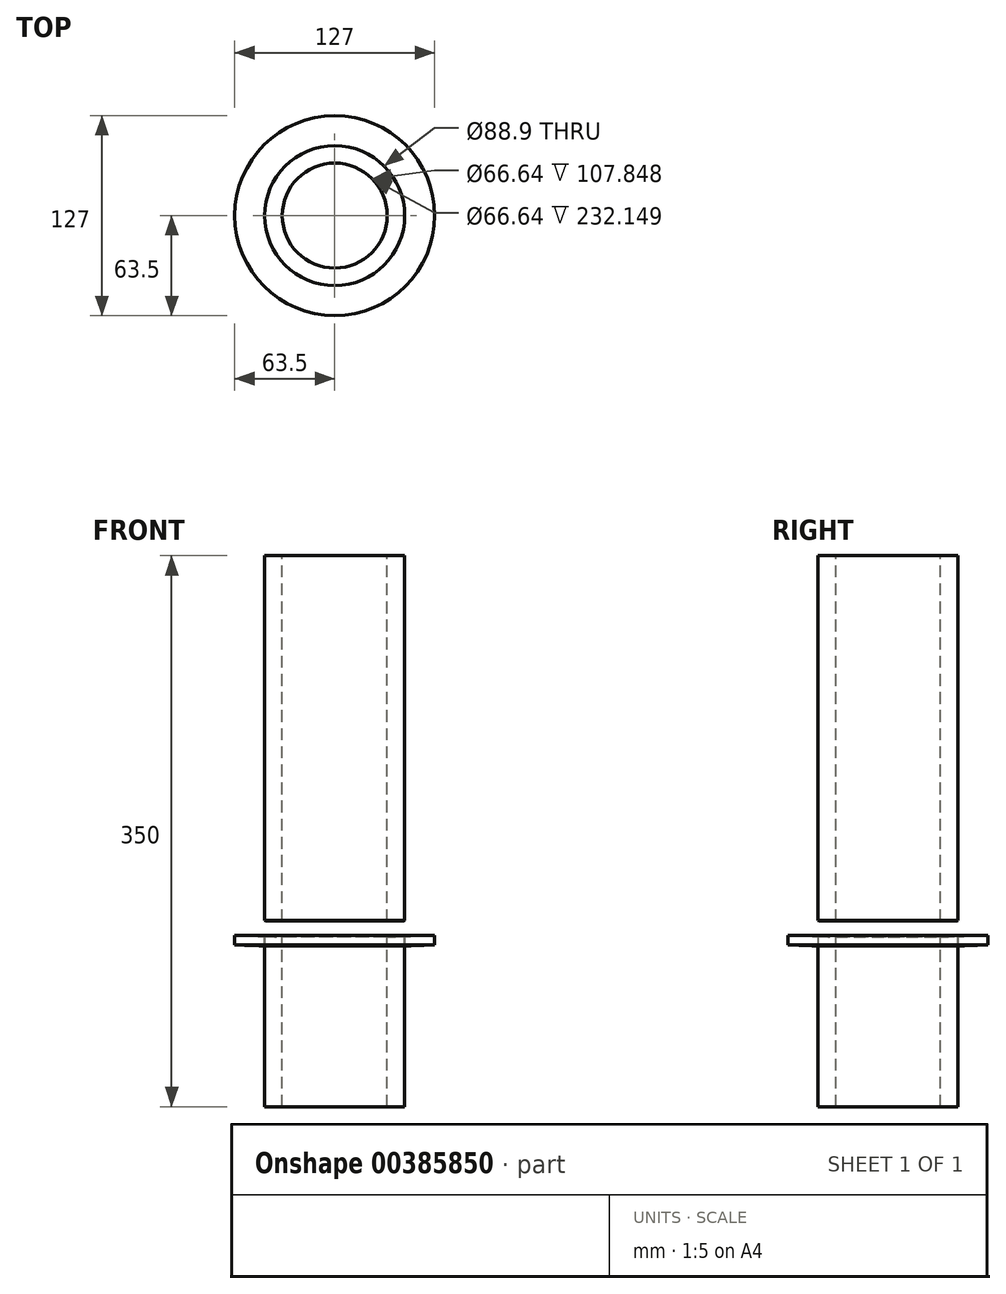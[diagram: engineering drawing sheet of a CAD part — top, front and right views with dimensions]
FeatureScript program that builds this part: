
annotation { "Feature Type Name" : "Feature", "Feature Type Description" : "" }
export const myFeature = defineFeature(function(context is Context, id is Id, definition is map)
    precondition{}
    {
        {
            var Q0;
            Q0=qCreatedBy(makeId("Front.planeOp"),FACE);
            var sketch = newSketch(context, id + "F0", { "sketchPlane" : qUnion([Q0])});
            skArc(sketch, "E0", {"start": v(-716, 0) * mm, "mid": v(-703.68, -44.35) * mm, "end": v(-670.25, -76) * mm});
            skLineSegment(sketch, "E1", {"start": v(0, -140.34) * mm, "end": v(0, 100.1) * mm, "construction": true});
            skArc(sketch, "E2.MirrorCS", {"start": v(716, 0) * mm, "mid": v(703.68, -44.35) * mm, "end": v(670.25, -76) * mm});
            skArc(sketch, "E3", {"start": v(-670.25, -76) * mm, "mid": v(0, -242.54) * mm, "end": v(670.25, -76) * mm});
            skLineSegment(sketch, "E4", {"start": v(716, 0) * mm, "end": v(-716, 0) * mm, "construction": true});
            skPoint(sketch, "E5.orphan", {"position": v(544, 0) * mm});
            skPoint(sketch, "E6.orphan", {"position": v(-544, 0) * mm});
            skLineSegment(sketch, "E7", {"start": v(716, 0) * mm, "end": v(716, 86) * mm});
            skLineSegment(sketch, "E8.MirrorCS", {"start": v(-716, 0) * mm, "end": v(-716, 81.96) * mm});
            skArc(sketch, "E9.0", {"start": v(-665.57, -67.16) * mm, "mid": v(0, -232.54) * mm, "end": v(665.57, -67.16) * mm});
            skArc(sketch, "E10.0", {"start": v(706, 0) * mm, "mid": v(695.11, -39.2) * mm, "end": v(665.57, -67.16) * mm});
            skLineSegment(sketch, "E11.0", {"start": v(706, 0) * mm, "end": v(706, 86) * mm});
            skArc(sketch, "E12.MirrorCS", {"start": v(-706, 0) * mm, "mid": v(-695.11, -39.2) * mm, "end": v(-665.57, -67.16) * mm});
            skLineSegment(sketch, "E13.MirrorCS", {"start": v(-706, 0) * mm, "end": v(-706, 86) * mm});
            skLineSegment(sketch, "E14", {"start": v(716, 86) * mm, "end": v(706, 86) * mm});
            skLineSegment(sketch, "E15.MirrorCS", {"start": v(-709, 86) * mm, "end": v(-706, 86) * mm});
            skLineSegment(sketch, "E16", {"start": v(0, -242.54) * mm, "end": v(0, -232.54) * mm});
            skLineSegment(sketch, "E17", {"start": v(-709, 86) * mm, "end": v(-716, 81.96) * mm});
            skPoint(sketch, "E18.orphan", {"position": v(-716, 86) * mm});
            skArc(sketch, "E19.0", {"start": v(44.45, -247.85) * mm, "mid": v(53.98, -247.53) * mm, "end": v(63.5, -247.14) * mm});
            skCircle(sketch, "E20", {"center": v(0, 0) * mm, "radius": 44.45 * mm, "construction": true});
            skCircle(sketch, "E21", {"center": v(0, 0) * mm, "radius": 63.5 * mm, "construction": true});
            skLineSegment(sketch, "E22", {"start": v(44.45, 0) * mm, "end": v(44.45, -241.85) * mm, "construction": true});
            skLineSegment(sketch, "E23", {"start": v(63.5, 0) * mm, "end": v(63.5, -241.13) * mm, "construction": true});
            skLineSegment(sketch, "E24", {"start": v(44.45, -241.85) * mm, "end": v(44.45, -247.85) * mm});
            skLineSegment(sketch, "E25", {"start": v(63.5, -241.13) * mm, "end": v(63.5, -247.14) * mm});
            skLineSegment(sketch, "E26", {"start": v(0, -232.54) * mm, "end": v(0, 0) * mm});
            skLineSegment(sketch, "E27", {"start": v(0, 0) * mm, "end": v(706, 0) * mm});
            skSolve(sketch);
        }
        {
            var Q0;
            Q0=makeQuery(id+"F0.imprint","IMPRINT",FACE,{"disambiguationData":[TD([[makeQuery(id+"F0.imprint","IMPRINT",EDGE,{"derivedFrom":sQuery(id+"F0.wireOp",EDGE,"E0")}),1.0]])]});
            var Q1;
            Q1=sQuery(id+"F0.wireOp",EDGE,"E1");
            revolve(context, id + "F1", {"entities" : qUnion([Q0]), "axis" : qUnion([Q1]), "revolveType" : RevolveType.FULL});
        }
        {
            var Q0;
            Q0=makeQuery(id+"F0.imprint","IMPRINT",FACE,{"disambiguationData":[TD([[makeQuery(id+"F0.imprint","IMPRINT",EDGE,{"derivedFrom":sQuery(id+"F0.wireOp",EDGE,"E19.0")}),1.0]])]});
            var Q1;
            Q1=sQuery(id+"F0.wireOp",EDGE,"E26");
            revolve(context, id + "F2", {"entities" : qUnion([Q0]), "axis" : qUnion([Q1]), "revolveType" : RevolveType.FULL});
        }
        {
            var Q0;
            Q0=qCreatedBy(makeId("Top.planeOp"),FACE);
            var sketch = newSketch(context, id + "F3", { "sketchPlane" : qUnion([Q0])});
            skCircle(sketch, "E28", {"center": v(0, 0) * mm, "radius": 44.45 * mm});
            skCircle(sketch, "E29", {"center": v(0, 0) * mm, "radius": 33.32 * mm});
            skSolve(sketch);
        }
        {
            var Q0;
            Q0=makeQuery(id+"F3.imprint","IMPRINT",FACE,{"disambiguationData":[TD([[makeQuery(id+"F3.imprint","IMPRINT",EDGE,{"derivedFrom":sQuery(id+"F3.wireOp",EDGE,"E29")}),1.0]])]});
            var Q1;
            Q1=makeQuery(id+"F3.imprint","IMPRINT",FACE,{"disambiguationData":[TD([[makeQuery(id+"F3.imprint","IMPRINT",EDGE,{"derivedFrom":sQuery(id+"F3.wireOp",EDGE,"E28")}),1.0]])]});
            extrude(context, id + "F4", {"entities" : qUnion([Q0, Q1]), "operationType" : NewBodyOperationType.REMOVE, "endBound" : BoundingType.THROUGH_ALL, "oppositeDirection" : true, "depth" : 25 * mm});
        }
        {
            var Q0;
            Q0=makeQuery(id+"F3.imprint","IMPRINT",FACE,{"disambiguationData":[TD([[makeQuery(id+"F3.imprint","IMPRINT",EDGE,{"derivedFrom":sQuery(id+"F3.wireOp",EDGE,"E28")}),1.0]])]});
            extrude(context, id + "F5", {"entities" : qUnion([Q0]), "oppositeDirection" : true, "depth" : 350 * mm});
        }
        {
            var Q0;
            {var subQ0=sQuery(id+"F0.wireOp",EDGE,"E10.0");Q0=makeQuery(id+"F0.imprint","IMPRINT",FACE,{"disambiguationData":[TD([[makeQuery(id+"F0.imprint","IMPRINT",EDGE,{"derivedFrom":subQ0}),-1.0]])]});}
            var Q1;
            Q1=sQuery(id+"F0.wireOp",EDGE,"E26");
            revolve(context, id + "F6", {"operationType" : NewBodyOperationType.REMOVE, "entities" : qUnion([Q0]), "axis" : qUnion([Q1]), "revolveType" : RevolveType.FULL, "oppositeDirection" : true});
        }
    });
